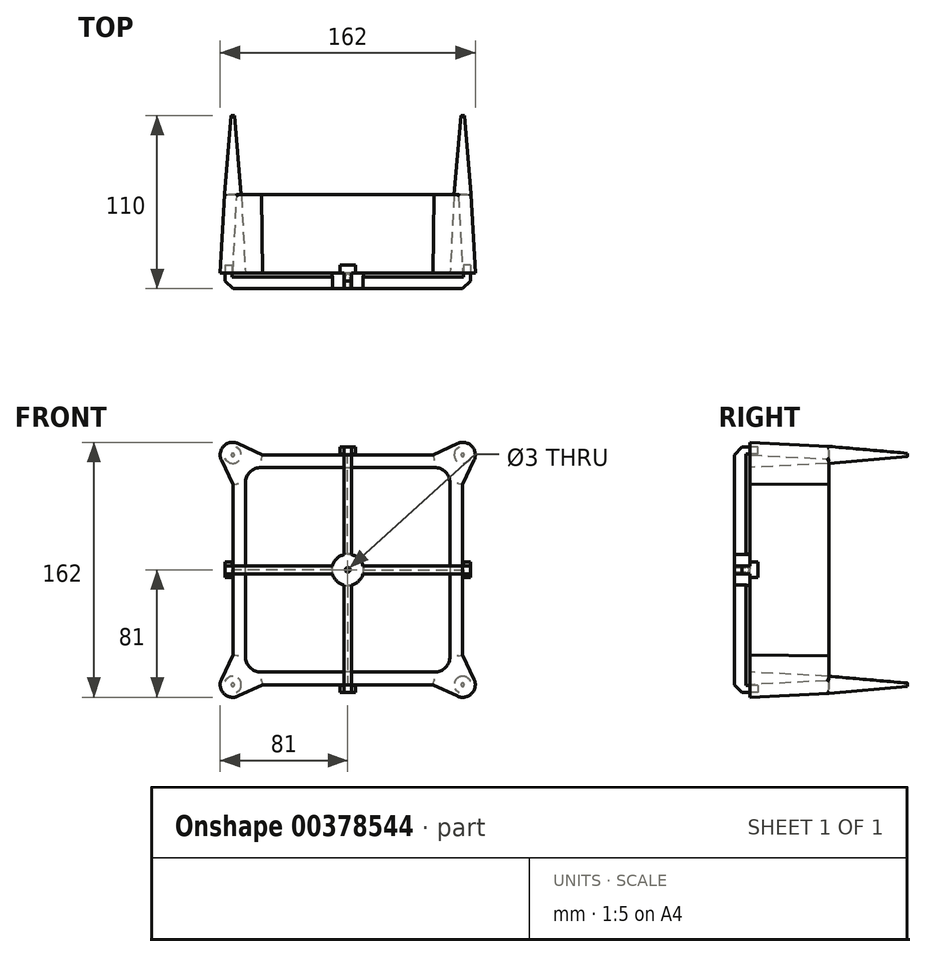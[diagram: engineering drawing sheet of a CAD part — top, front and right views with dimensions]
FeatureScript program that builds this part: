
annotation { "Feature Type Name" : "Feature", "Feature Type Description" : "" }
export const myFeature = defineFeature(function(context is Context, id is Id, definition is map)
    precondition{}
    {
        {
            var Q0;
            Q0=qCreatedBy(makeId("Front.planeOp"),FACE);
            var sketch = newSketch(context, id + "F0", { "sketchPlane" : qUnion([Q0])});
            skLineSegment(sketch, "E0.right", {"start": v(-73, 54.07) * mm, "end": v(-73, 0) * mm});
            skPoint(sketch, "E0.middle", {"position": v(0, 0) * mm});
            skLineSegment(sketch, "E1.bottom", {"start": v(0, 65) * mm, "end": v(-55, 65) * mm});
            skLineSegment(sketch, "E1.right", {"start": v(-65, 55) * mm, "end": v(-65, 0) * mm});
            skPoint(sketch, "E2.visualSharp", {"position": v(-65, 65) * mm});
            skArc(sketch, "E2.filletArc", {"start": v(-55, 65) * mm, "mid": v(-62.07, 62.07) * mm, "end": v(-65, 55) * mm});
            skPoint(sketch, "E3.visualSharp", {"position": v(-73, 73) * mm});
            skArc(sketch, "E4", {"start": v(-69.62, 80.25) * mm, "mid": v(-78.66, 78.66) * mm, "end": v(-80.25, 69.62) * mm});
            skLineSegment(sketch, "E5", {"start": v(-54.07, 73) * mm, "end": v(-69.62, 80.25) * mm});
            skLineSegment(sketch, "E6", {"start": v(-73, 54.07) * mm, "end": v(-80.25, 69.62) * mm});
            skLineSegment(sketch, "E7", {"start": v(-65, 0) * mm, "end": v(-73, 0) * mm});
            skLineSegment(sketch, "E8", {"start": v(0, 73) * mm, "end": v(0, 65) * mm});
            skLineSegment(sketch, "E9.trimOffspring", {"start": v(0, 73) * mm, "end": v(-54.07, 73) * mm});
            skLineSegment(sketch, "E10.MirrorCS", {"start": v(0, 73) * mm, "end": v(54.07, 73) * mm});
            skLineSegment(sketch, "E11.MirrorCS", {"start": v(65, 0) * mm, "end": v(73, 0) * mm});
            skLineSegment(sketch, "E12.MirrorCS", {"start": v(73, 54.07) * mm, "end": v(80.25, 69.62) * mm});
            skLineSegment(sketch, "E13.MirrorCS", {"start": v(54.07, 73) * mm, "end": v(69.62, 80.25) * mm});
            skLineSegment(sketch, "E14.MirrorCS", {"start": v(73, 54.07) * mm, "end": v(73, 0) * mm});
            skLineSegment(sketch, "E15.MirrorCS", {"start": v(65, 55) * mm, "end": v(65, 0) * mm});
            skLineSegment(sketch, "E16.MirrorCS", {"start": v(0, 65) * mm, "end": v(55, 65) * mm});
            skPoint(sketch, "E17.MirrorP", {"position": v(73, 73) * mm});
            skPoint(sketch, "E18.MirrorP", {"position": v(65, 65) * mm});
            skArc(sketch, "E19.MirrorCS", {"start": v(69.62, 80.25) * mm, "mid": v(78.66, 78.66) * mm, "end": v(80.25, 69.62) * mm});
            skArc(sketch, "E20.MirrorCS", {"start": v(55, 65) * mm, "mid": v(62.07, 62.07) * mm, "end": v(65, 55) * mm});
            skLineSegment(sketch, "E21.MirrorCS", {"start": v(65, -55) * mm, "end": v(65, 0) * mm});
            skLineSegment(sketch, "E22.MirrorCS", {"start": v(0, -73) * mm, "end": v(0, -65) * mm});
            skLineSegment(sketch, "E23.MirrorCS", {"start": v(0, -65) * mm, "end": v(-55, -65) * mm});
            skPoint(sketch, "E24.MirrorP", {"position": v(-73, -73) * mm});
            skArc(sketch, "E25.MirrorCS", {"start": v(-69.62, -80.25) * mm, "mid": v(-78.66, -78.66) * mm, "end": v(-80.25, -69.62) * mm});
            skLineSegment(sketch, "E26.MirrorCS", {"start": v(-65, -55) * mm, "end": v(-65, 0) * mm});
            skPoint(sketch, "E27.MirrorP", {"position": v(73, -73) * mm});
            skLineSegment(sketch, "E28.MirrorCS", {"start": v(0, -65) * mm, "end": v(55, -65) * mm});
            skLineSegment(sketch, "E29.MirrorCS", {"start": v(54.07, -73) * mm, "end": v(69.62, -80.25) * mm});
            skLineSegment(sketch, "E30.MirrorCS", {"start": v(-54.07, -73) * mm, "end": v(-69.62, -80.25) * mm});
            skArc(sketch, "E31.MirrorCS", {"start": v(69.62, -80.25) * mm, "mid": v(78.66, -78.66) * mm, "end": v(80.25, -69.62) * mm});
            skLineSegment(sketch, "E32.MirrorCS", {"start": v(-73, -54.07) * mm, "end": v(-73, 0) * mm});
            skArc(sketch, "E33.MirrorCS", {"start": v(-55, -65) * mm, "mid": v(-62.07, -62.07) * mm, "end": v(-65, -55) * mm});
            skLineSegment(sketch, "E34.MirrorCS", {"start": v(0, -73) * mm, "end": v(-54.07, -73) * mm});
            skPoint(sketch, "E35.MirrorP", {"position": v(65, -65) * mm});
            skLineSegment(sketch, "E36.MirrorCS", {"start": v(0, -73) * mm, "end": v(54.07, -73) * mm});
            skLineSegment(sketch, "E37.MirrorCS", {"start": v(-73, -54.07) * mm, "end": v(-80.25, -69.62) * mm});
            skArc(sketch, "E38.MirrorCS", {"start": v(55, -65) * mm, "mid": v(62.07, -62.07) * mm, "end": v(65, -55) * mm});
            skPoint(sketch, "E39.MirrorP", {"position": v(-65, -65) * mm});
            skLineSegment(sketch, "E40.MirrorCS", {"start": v(73, -54.07) * mm, "end": v(73, 0) * mm});
            skLineSegment(sketch, "E41.MirrorCS", {"start": v(73, -54.07) * mm, "end": v(80.25, -69.62) * mm});
            skSolve(sketch);
        }
        {
            var Q0;
            Q0 = qSketchRegion(id + "F0", true);
            extrude(context, id + "F1", {"entities" : qUnion([Q0]), "oppositeDirection" : true, "depth" : 50 * mm, "hasDraft" : true, "draftAngle" : 3 * degree, "draftPullDirection" : true});
        }
        {
            var Q0;
            Q0=makeQuery(id+"F1.opExtrude","CAP_FACE",FACE,{"disambiguationData":[OSD([sQuery(id+"F0.wireOp",EDGE,"E0.right"),sQuery(id+"F0.wireOp",EDGE,"E1.bottom"),sQuery(id+"F0.wireOp",EDGE,"E1.right"),sQuery(id+"F0.wireOp",EDGE,"E2.filletArc"),sQuery(id+"F0.wireOp",EDGE,"E4"),sQuery(id+"F0.wireOp",EDGE,"E5"),sQuery(id+"F0.wireOp",EDGE,"E6"),sQuery(id+"F0.wireOp",EDGE,"E9.trimOffspring"),sQuery(id+"F0.wireOp",EDGE,"E10.MirrorCS"),sQuery(id+"F0.wireOp",EDGE,"E12.MirrorCS"),sQuery(id+"F0.wireOp",EDGE,"E13.MirrorCS"),sQuery(id+"F0.wireOp",EDGE,"E14.MirrorCS"),sQuery(id+"F0.wireOp",EDGE,"E15.MirrorCS"),sQuery(id+"F0.wireOp",EDGE,"E16.MirrorCS"),sQuery(id+"F0.wireOp",EDGE,"E19.MirrorCS"),sQuery(id+"F0.wireOp",EDGE,"E20.MirrorCS"),sQuery(id+"F0.wireOp",EDGE,"E21.MirrorCS"),sQuery(id+"F0.wireOp",EDGE,"E23.MirrorCS"),sQuery(id+"F0.wireOp",EDGE,"E25.MirrorCS"),sQuery(id+"F0.wireOp",EDGE,"E26.MirrorCS"),sQuery(id+"F0.wireOp",EDGE,"E28.MirrorCS"),sQuery(id+"F0.wireOp",EDGE,"E29.MirrorCS"),sQuery(id+"F0.wireOp",EDGE,"E30.MirrorCS"),sQuery(id+"F0.wireOp",EDGE,"E31.MirrorCS"),sQuery(id+"F0.wireOp",EDGE,"E32.MirrorCS"),sQuery(id+"F0.wireOp",EDGE,"E33.MirrorCS"),sQuery(id+"F0.wireOp",EDGE,"E34.MirrorCS"),sQuery(id+"F0.wireOp",EDGE,"E36.MirrorCS"),sQuery(id+"F0.wireOp",EDGE,"E37.MirrorCS"),sQuery(id+"F0.wireOp",EDGE,"E38.MirrorCS"),sQuery(id+"F0.wireOp",EDGE,"E40.MirrorCS"),sQuery(id+"F0.wireOp",EDGE,"E41.MirrorCS")])],"isStart":false});
            var sketch = newSketch(context, id + "F2", { "sketchPlane" : qUnion([Q0])});
            skCircle(sketch, "E42", {"center": v(-73, -73) * mm, "radius": 5.38 * mm});
            skCircle(sketch, "E43", {"center": v(73, -73) * mm, "radius": 5.38 * mm});
            skCircle(sketch, "E44", {"center": v(-73, 73) * mm, "radius": 5.38 * mm});
            skCircle(sketch, "E45", {"center": v(73, 73) * mm, "radius": 5.38 * mm});
            skSolve(sketch);
        }
        {
            var Q0;
            Q0 = qSketchRegion(id + "F2", true);
            extrude(context, id + "F3", {"entities" : qUnion([Q0]), "operationType" : NewBodyOperationType.ADD, "depth" : 50 * mm, "hasDraft" : true, "draftAngle" : 5 * degree, "draftPullDirection" : true});
        }
        {
            var Q0;
            Q0=makeQuery(id+"F1.opExtrude","CAP_EDGE",EDGE,{"disambiguationData":[OSD([sQuery(id+"F0.wireOp",EDGE,"E23.MirrorCS"),sQuery(id+"F0.wireOp",EDGE,"E28.MirrorCS")])],"isStart":false});
            var Q1;
            Q1=makeQuery(id+"F1.opExtrude","CAP_EDGE",EDGE,{"disambiguationData":[OSD([sQuery(id+"F0.wireOp",EDGE,"E34.MirrorCS"),sQuery(id+"F0.wireOp",EDGE,"E36.MirrorCS")])],"isStart":false});
            var Q2;
            Q2=makeQuery(id+"F1.opExtrude","CAP_EDGE",EDGE,{"disambiguationData":[OSD([sQuery(id+"F0.wireOp",EDGE,"E30.MirrorCS")])],"isStart":false});
            var Q3;
            Q3=makeQuery(id+"F1.opExtrude","CAP_EDGE",EDGE,{"disambiguationData":[OSD([sQuery(id+"F0.wireOp",EDGE,"E0.right"),sQuery(id+"F0.wireOp",EDGE,"E32.MirrorCS")])],"isStart":false});
            var Q4;
            Q4=makeQuery(id+"F1.opExtrude","CAP_EDGE",EDGE,{"disambiguationData":[OSD([sQuery(id+"F0.wireOp",EDGE,"E6")])],"isStart":false});
            var Q5;
            Q5=makeQuery(id+"F1.opExtrude","CAP_EDGE",EDGE,{"disambiguationData":[OSD([sQuery(id+"F0.wireOp",EDGE,"E5")])],"isStart":false});
            var Q6;
            Q6=makeQuery(id+"F1.opExtrude","CAP_EDGE",EDGE,{"disambiguationData":[OSD([sQuery(id+"F0.wireOp",EDGE,"E9.trimOffspring"),sQuery(id+"F0.wireOp",EDGE,"E10.MirrorCS")])],"isStart":false});
            var Q7;
            Q7=makeQuery(id+"F1.opExtrude","CAP_EDGE",EDGE,{"disambiguationData":[OSD([sQuery(id+"F0.wireOp",EDGE,"E13.MirrorCS")])],"isStart":false});
            var Q8;
            Q8=makeQuery(id+"F1.opExtrude","CAP_EDGE",EDGE,{"disambiguationData":[OSD([sQuery(id+"F0.wireOp",EDGE,"E12.MirrorCS")])],"isStart":false});
            var Q9;
            Q9=makeQuery(id+"F1.opExtrude","CAP_EDGE",EDGE,{"disambiguationData":[OSD([sQuery(id+"F0.wireOp",EDGE,"E14.MirrorCS"),sQuery(id+"F0.wireOp",EDGE,"E40.MirrorCS")])],"isStart":false});
            var Q10;
            Q10=makeQuery(id+"F1.opExtrude","CAP_EDGE",EDGE,{"disambiguationData":[OSD([sQuery(id+"F0.wireOp",EDGE,"E29.MirrorCS")])],"isStart":false});
            var Q11;
            Q11=makeQuery(id+"F1.opExtrude","CAP_EDGE",EDGE,{"disambiguationData":[OSD([sQuery(id+"F0.wireOp",EDGE,"E41.MirrorCS")])],"isStart":false});
            var Q12;
            Q12=makeQuery(id+"F1.opExtrude","CAP_EDGE",EDGE,{"disambiguationData":[OSD([sQuery(id+"F0.wireOp",EDGE,"E37.MirrorCS")])],"isStart":false});
            fillet(context, id + "F4", {"entities" : qUnion([Q0, Q1, Q2, Q3, Q4, Q5, Q6, Q7, Q8, Q9, Q10, Q11, Q12]), "radius" : 1 * mm, "tangentPropagation" : true, "allowEdgeOverflow" : false});
        }
        {
            var Q0;
            Q0=makeQuery(id+"F1.opExtrude","CAP_FACE",FACE,{"disambiguationData":[OSD([sQuery(id+"F0.wireOp",EDGE,"E0.right"),sQuery(id+"F0.wireOp",EDGE,"E1.bottom"),sQuery(id+"F0.wireOp",EDGE,"E1.right"),sQuery(id+"F0.wireOp",EDGE,"E2.filletArc"),sQuery(id+"F0.wireOp",EDGE,"E4"),sQuery(id+"F0.wireOp",EDGE,"E5"),sQuery(id+"F0.wireOp",EDGE,"E6"),sQuery(id+"F0.wireOp",EDGE,"E9.trimOffspring"),sQuery(id+"F0.wireOp",EDGE,"E10.MirrorCS"),sQuery(id+"F0.wireOp",EDGE,"E12.MirrorCS"),sQuery(id+"F0.wireOp",EDGE,"E13.MirrorCS"),sQuery(id+"F0.wireOp",EDGE,"E14.MirrorCS"),sQuery(id+"F0.wireOp",EDGE,"E15.MirrorCS"),sQuery(id+"F0.wireOp",EDGE,"E16.MirrorCS"),sQuery(id+"F0.wireOp",EDGE,"E19.MirrorCS"),sQuery(id+"F0.wireOp",EDGE,"E20.MirrorCS"),sQuery(id+"F0.wireOp",EDGE,"E21.MirrorCS"),sQuery(id+"F0.wireOp",EDGE,"E23.MirrorCS"),sQuery(id+"F0.wireOp",EDGE,"E25.MirrorCS"),sQuery(id+"F0.wireOp",EDGE,"E26.MirrorCS"),sQuery(id+"F0.wireOp",EDGE,"E28.MirrorCS"),sQuery(id+"F0.wireOp",EDGE,"E29.MirrorCS"),sQuery(id+"F0.wireOp",EDGE,"E30.MirrorCS"),sQuery(id+"F0.wireOp",EDGE,"E31.MirrorCS"),sQuery(id+"F0.wireOp",EDGE,"E32.MirrorCS"),sQuery(id+"F0.wireOp",EDGE,"E33.MirrorCS"),sQuery(id+"F0.wireOp",EDGE,"E34.MirrorCS"),sQuery(id+"F0.wireOp",EDGE,"E36.MirrorCS"),sQuery(id+"F0.wireOp",EDGE,"E37.MirrorCS"),sQuery(id+"F0.wireOp",EDGE,"E38.MirrorCS"),sQuery(id+"F0.wireOp",EDGE,"E40.MirrorCS"),sQuery(id+"F0.wireOp",EDGE,"E41.MirrorCS")])],"isStart":true});
            var sketch = newSketch(context, id + "F5", { "sketchPlane" : qUnion([Q0])});
            skPoint(sketch, "E46.firstSnap0", {"position": v(-61.84, 76.63) * mm});
            skLineSegment(sketch, "E46.bottom", {"start": v(-2.5, 78) * mm, "end": v(2.5, 78) * mm});
            skLineSegment(sketch, "E46.top", {"start": v(-2.5, -78) * mm, "end": v(2.5, -78) * mm});
            skLineSegment(sketch, "E46.left", {"start": v(-2.5, 78) * mm, "end": v(-2.5, 9.68) * mm});
            skLineSegment(sketch, "E46.right", {"start": v(2.5, 78) * mm, "end": v(2.5, 9.68) * mm});
            skLineSegment(sketch, "E47.bottom", {"start": v(-78, 2.5) * mm, "end": v(-9.68, 2.5) * mm});
            skLineSegment(sketch, "E47.top", {"start": v(-78, -2.5) * mm, "end": v(-9.68, -2.5) * mm});
            skLineSegment(sketch, "E47.left", {"start": v(-78, 2.5) * mm, "end": v(-78, -2.5) * mm});
            skLineSegment(sketch, "E47.right", {"start": v(78, 2.5) * mm, "end": v(78, -2.5) * mm});
            skArc(sketch, "E48", {"start": v(-2.5, 9.68) * mm, "mid": v(-7.07, 7.07) * mm, "end": v(-9.68, 2.5) * mm});
            skLineSegment(sketch, "E49.trimOffspring", {"start": v(9.68, 2.5) * mm, "end": v(78, 2.5) * mm});
            skLineSegment(sketch, "E50.trimOffspring", {"start": v(9.68, -2.5) * mm, "end": v(78, -2.5) * mm});
            skLineSegment(sketch, "E51.trimOffspring", {"start": v(2.5, -9.68) * mm, "end": v(2.5, -78) * mm});
            skLineSegment(sketch, "E52.trimOffspring", {"start": v(-2.5, -9.68) * mm, "end": v(-2.5, -78) * mm});
            skArc(sketch, "E53.trimOffspring", {"start": v(-9.68, -2.5) * mm, "mid": v(-7.07, -7.07) * mm, "end": v(-2.5, -9.68) * mm});
            skArc(sketch, "E54.trimOffspring", {"start": v(2.5, -9.68) * mm, "mid": v(7.07, -7.07) * mm, "end": v(9.68, -2.5) * mm});
            skArc(sketch, "E55.trimOffspring", {"start": v(9.68, 2.5) * mm, "mid": v(7.07, 7.07) * mm, "end": v(2.5, 9.68) * mm});
            skCircle(sketch, "E56", {"center": v(0, 0) * mm, "radius": 1.5 * mm});
            skSolve(sketch);
        }
        {
            var Q0;
            Q0 = qSketchRegion(id + "F5", true);
            extrude(context, id + "F6", {"entities" : qUnion([Q0]), "depth" : 10 * mm});
        }
        {
            var Q0;
            Q0=makeQuery(id+"F6.opExtrude","CAP_FACE",FACE,{"disambiguationData":[OSD([sQuery(id+"F5.wireOp",EDGE,"E46.bottom"),sQuery(id+"F5.wireOp",EDGE,"E46.top"),sQuery(id+"F5.wireOp",EDGE,"E46.left"),sQuery(id+"F5.wireOp",EDGE,"E46.right"),sQuery(id+"F5.wireOp",EDGE,"E47.bottom"),sQuery(id+"F5.wireOp",EDGE,"E47.top"),sQuery(id+"F5.wireOp",EDGE,"E47.left"),sQuery(id+"F5.wireOp",EDGE,"E47.right"),sQuery(id+"F5.wireOp",EDGE,"E48"),sQuery(id+"F5.wireOp",EDGE,"E49.trimOffspring"),sQuery(id+"F5.wireOp",EDGE,"E50.trimOffspring"),sQuery(id+"F5.wireOp",EDGE,"E51.trimOffspring"),sQuery(id+"F5.wireOp",EDGE,"E52.trimOffspring"),sQuery(id+"F5.wireOp",EDGE,"E53.trimOffspring"),sQuery(id+"F5.wireOp",EDGE,"E54.trimOffspring"),sQuery(id+"F5.wireOp",EDGE,"E55.trimOffspring"),sQuery(id+"F5.wireOp",EDGE,"E56")])],"isStart":true});
            var sketch = newSketch(context, id + "F7", { "sketchPlane" : qUnion([Q0])});
            skLineSegment(sketch, "E57.bottom", {"start": v(78, 5) * mm, "end": v(73.5, 5) * mm});
            skLineSegment(sketch, "E57.top", {"start": v(78, -5) * mm, "end": v(73.5, -5) * mm});
            skLineSegment(sketch, "E57.left", {"start": v(78, 5) * mm, "end": v(78, -5) * mm});
            skLineSegment(sketch, "E57.right", {"start": v(73.5, 5) * mm, "end": v(73.5, -5) * mm});
            skLineSegment(sketch, "E58.bottom", {"start": v(5, -73.5) * mm, "end": v(-5, -73.5) * mm});
            skLineSegment(sketch, "E58.top", {"start": v(5, -78) * mm, "end": v(-5, -78) * mm});
            skLineSegment(sketch, "E58.left", {"start": v(5, -73.5) * mm, "end": v(5, -78) * mm});
            skLineSegment(sketch, "E58.right", {"start": v(-5, -73.5) * mm, "end": v(-5, -78) * mm});
            skLineSegment(sketch, "E59.bottom", {"start": v(-78, -5) * mm, "end": v(-73.5, -5) * mm});
            skLineSegment(sketch, "E59.top", {"start": v(-78, 5) * mm, "end": v(-73.5, 5) * mm});
            skLineSegment(sketch, "E59.left", {"start": v(-78, -5) * mm, "end": v(-78, 5) * mm});
            skLineSegment(sketch, "E59.right", {"start": v(-73.5, -5) * mm, "end": v(-73.5, 5) * mm});
            skLineSegment(sketch, "E60.bottom", {"start": v(-5, 73.5) * mm, "end": v(5, 73.5) * mm});
            skLineSegment(sketch, "E60.top", {"start": v(-5, 78) * mm, "end": v(5, 78) * mm});
            skLineSegment(sketch, "E60.left", {"start": v(-5, 73.5) * mm, "end": v(-5, 78) * mm});
            skLineSegment(sketch, "E60.right", {"start": v(5, 73.5) * mm, "end": v(5, 78) * mm});
            skSolve(sketch);
        }
        {
            var Q0;
            Q0 = qSketchRegion(id + "F7", true);
            extrude(context, id + "F8", {"entities" : qUnion([Q0]), "operationType" : NewBodyOperationType.ADD, "depth" : 5 * mm});
        }
        {
            var Q0;
            {var subQ0=sQuery(id+"F5.wireOp",EDGE,"E49.trimOffspring");Q0=makeQuery(id+"F8.boolean.opBoolean","SPLIT",EDGE,{"disambiguationData":[topologyDisambiguationEdgeConnected([makeQuery(id+"F8.opExtrude","CAP_FACE",FACE,{"disambiguationData":[OSD([sQuery(id+"F7.wireOp",EDGE,"E59.bottom"),sQuery(id+"F7.wireOp",EDGE,"E59.top"),sQuery(id+"F7.wireOp",EDGE,"E59.left"),sQuery(id+"F7.wireOp",EDGE,"E59.right")])],"isStart":true})])],"derivedFrom":makeQuery(id+"F6.opExtrude","CAP_EDGE",EDGE,{"disambiguationData":[OSD([subQ0])],"isStart":true})});}
            var Q1;
            {var subQ0=sQuery(id+"F5.wireOp",EDGE,"E50.trimOffspring");Q1=makeQuery(id+"F8.boolean.opBoolean","SPLIT",EDGE,{"disambiguationData":[topologyDisambiguationEdgeConnected([makeQuery(id+"F8.opExtrude","CAP_FACE",FACE,{"disambiguationData":[OSD([sQuery(id+"F7.wireOp",EDGE,"E59.bottom"),sQuery(id+"F7.wireOp",EDGE,"E59.top"),sQuery(id+"F7.wireOp",EDGE,"E59.left"),sQuery(id+"F7.wireOp",EDGE,"E59.right")])],"isStart":true})])],"derivedFrom":makeQuery(id+"F6.opExtrude","CAP_EDGE",EDGE,{"disambiguationData":[OSD([subQ0])],"isStart":true})});}
            var Q2;
            {var subQ0=sQuery(id+"F5.wireOp",EDGE,"E46.right");Q2=makeQuery(id+"F8.boolean.opBoolean","SPLIT",EDGE,{"disambiguationData":[topologyDisambiguationEdgeConnected([makeQuery(id+"F8.opExtrude","CAP_FACE",FACE,{"disambiguationData":[OSD([sQuery(id+"F7.wireOp",EDGE,"E60.bottom"),sQuery(id+"F7.wireOp",EDGE,"E60.top"),sQuery(id+"F7.wireOp",EDGE,"E60.left"),sQuery(id+"F7.wireOp",EDGE,"E60.right")])],"isStart":true})])],"derivedFrom":makeQuery(id+"F6.opExtrude","CAP_EDGE",EDGE,{"disambiguationData":[OSD([subQ0])],"isStart":true})});}
            var Q3;
            {var subQ0=sQuery(id+"F5.wireOp",EDGE,"E46.left");Q3=makeQuery(id+"F8.boolean.opBoolean","SPLIT",EDGE,{"disambiguationData":[topologyDisambiguationEdgeConnected([makeQuery(id+"F8.opExtrude","CAP_FACE",FACE,{"disambiguationData":[OSD([sQuery(id+"F7.wireOp",EDGE,"E60.bottom"),sQuery(id+"F7.wireOp",EDGE,"E60.top"),sQuery(id+"F7.wireOp",EDGE,"E60.left"),sQuery(id+"F7.wireOp",EDGE,"E60.right")])],"isStart":true})])],"derivedFrom":makeQuery(id+"F6.opExtrude","CAP_EDGE",EDGE,{"disambiguationData":[OSD([subQ0])],"isStart":true})});}
            var Q4;
            {var subQ0=sQuery(id+"F5.wireOp",EDGE,"E47.top");Q4=makeQuery(id+"F8.boolean.opBoolean","SPLIT",EDGE,{"disambiguationData":[topologyDisambiguationEdgeConnected([makeQuery(id+"F8.opExtrude","CAP_FACE",FACE,{"disambiguationData":[OSD([sQuery(id+"F7.wireOp",EDGE,"E57.bottom"),sQuery(id+"F7.wireOp",EDGE,"E57.top"),sQuery(id+"F7.wireOp",EDGE,"E57.left"),sQuery(id+"F7.wireOp",EDGE,"E57.right")])],"isStart":true})])],"derivedFrom":makeQuery(id+"F6.opExtrude","CAP_EDGE",EDGE,{"disambiguationData":[OSD([subQ0])],"isStart":true})});}
            var Q5;
            {var subQ0=sQuery(id+"F5.wireOp",EDGE,"E47.bottom");Q5=makeQuery(id+"F8.boolean.opBoolean","SPLIT",EDGE,{"disambiguationData":[topologyDisambiguationEdgeConnected([makeQuery(id+"F8.opExtrude","CAP_FACE",FACE,{"disambiguationData":[OSD([sQuery(id+"F7.wireOp",EDGE,"E57.bottom"),sQuery(id+"F7.wireOp",EDGE,"E57.top"),sQuery(id+"F7.wireOp",EDGE,"E57.left"),sQuery(id+"F7.wireOp",EDGE,"E57.right")])],"isStart":true})])],"derivedFrom":makeQuery(id+"F6.opExtrude","CAP_EDGE",EDGE,{"disambiguationData":[OSD([subQ0])],"isStart":true})});}
            var Q6;
            {var subQ0=sQuery(id+"F5.wireOp",EDGE,"E52.trimOffspring");Q6=makeQuery(id+"F8.boolean.opBoolean","SPLIT",EDGE,{"disambiguationData":[topologyDisambiguationEdgeConnected([makeQuery(id+"F8.opExtrude","CAP_FACE",FACE,{"disambiguationData":[OSD([sQuery(id+"F7.wireOp",EDGE,"E58.bottom"),sQuery(id+"F7.wireOp",EDGE,"E58.top"),sQuery(id+"F7.wireOp",EDGE,"E58.left"),sQuery(id+"F7.wireOp",EDGE,"E58.right")])],"isStart":true})])],"derivedFrom":makeQuery(id+"F6.opExtrude","CAP_EDGE",EDGE,{"disambiguationData":[OSD([subQ0])],"isStart":true})});}
            var Q7;
            {var subQ0=sQuery(id+"F5.wireOp",EDGE,"E51.trimOffspring");Q7=makeQuery(id+"F8.boolean.opBoolean","SPLIT",EDGE,{"disambiguationData":[topologyDisambiguationEdgeConnected([makeQuery(id+"F8.opExtrude","CAP_FACE",FACE,{"disambiguationData":[OSD([sQuery(id+"F7.wireOp",EDGE,"E58.bottom"),sQuery(id+"F7.wireOp",EDGE,"E58.top"),sQuery(id+"F7.wireOp",EDGE,"E58.left"),sQuery(id+"F7.wireOp",EDGE,"E58.right")])],"isStart":true})])],"derivedFrom":makeQuery(id+"F6.opExtrude","CAP_EDGE",EDGE,{"disambiguationData":[OSD([subQ0])],"isStart":true})});}
            chamfer(context, id + "F9", {"entities" : qUnion([Q0, Q1, Q2, Q3, Q4, Q5, Q6, Q7]), "width" : 2.5 * mm, "tangentPropagation" : true});
        }
        {
            var Q0;
            Q0=makeQuery(id+"F6.opExtrude","CAP_EDGE",EDGE,{"disambiguationData":[OSD([sQuery(id+"F5.wireOp",EDGE,"E46.bottom")])],"isStart":false});
            var Q1;
            Q1=makeQuery(id+"F6.opExtrude","CAP_EDGE",EDGE,{"disambiguationData":[OSD([sQuery(id+"F5.wireOp",EDGE,"E47.left")])],"isStart":false});
            var Q2;
            Q2=makeQuery(id+"F6.opExtrude","CAP_EDGE",EDGE,{"disambiguationData":[OSD([sQuery(id+"F5.wireOp",EDGE,"E46.top")])],"isStart":false});
            var Q3;
            Q3=makeQuery(id+"F6.opExtrude","CAP_EDGE",EDGE,{"disambiguationData":[OSD([sQuery(id+"F5.wireOp",EDGE,"E47.right")])],"isStart":false});
            chamfer(context, id + "F10", {"entities" : qUnion([Q0, Q1, Q2, Q3]), "width" : 5 * mm, "tangentPropagation" : true});
        }
    });
